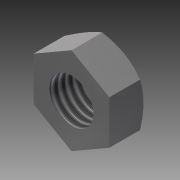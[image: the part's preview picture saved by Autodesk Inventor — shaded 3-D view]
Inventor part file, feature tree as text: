
AUTODESK INVENTOR PART (.ipt)
format: ipt  version: 2013 (Build 170138000, 138)  size: 105,472 bytes
history: native  units: mm
features: sketch x2, other x1, revolve x1, extrude x1, thread x1
ambient origin geometry x1: Origin
feature tree (6):
  other  "ソリッド1"
  revolve  "回転1"
  extrude  "押し出し1"  Depth=1.2mm
  thread  "ねじ1"
  sketch  "スケッチ1"
  sketch  "スケッチ2"
